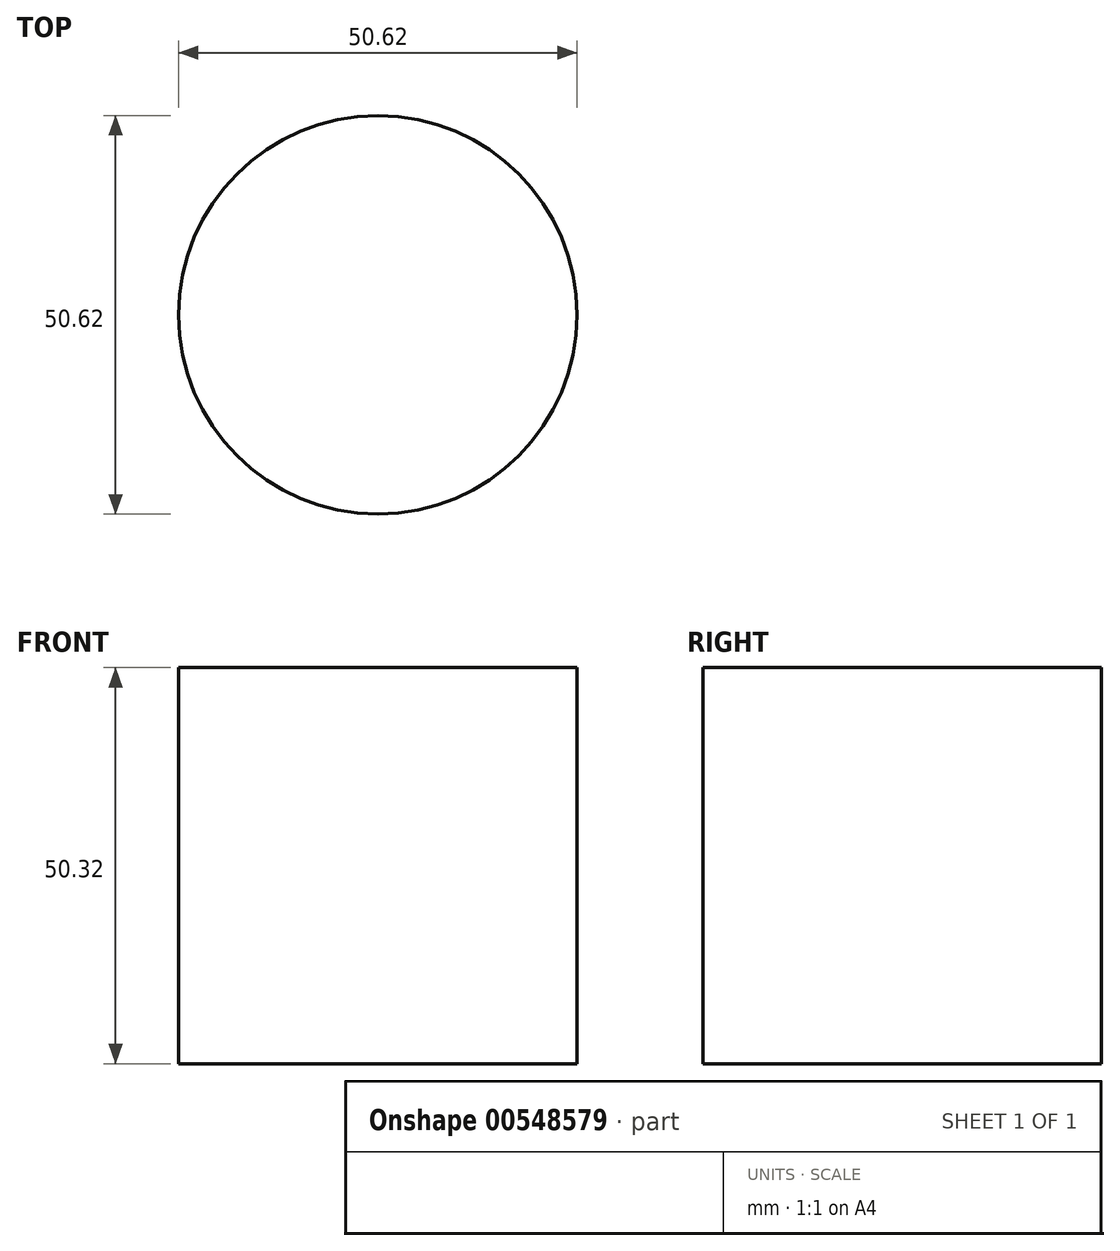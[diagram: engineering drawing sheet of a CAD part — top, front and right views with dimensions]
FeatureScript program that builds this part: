
annotation { "Feature Type Name" : "Feature", "Feature Type Description" : "" }
export const myFeature = defineFeature(function(context is Context, id is Id, definition is map)
    precondition{}
    {
        {
            var Q0;
            Q0=qCreatedBy(makeId("Front.planeOp"),FACE);
            var sketch = newSketch(context, id + "F0", { "sketchPlane" : qUnion([Q0])});
            skLineSegment(sketch, "E0.bottom", {"start": v(0, 25.16) * mm, "end": v(25.31, 25.16) * mm});
            skLineSegment(sketch, "E0.top", {"start": v(0, -25.16) * mm, "end": v(25.31, -25.16) * mm});
            skLineSegment(sketch, "E0.left", {"start": v(0, 25.16) * mm, "end": v(0, -25.16) * mm});
            skLineSegment(sketch, "E0.right", {"start": v(25.31, 25.16) * mm, "end": v(25.31, -25.16) * mm});
            skLineSegment(sketch, "E1", {"start": v(0, 42.63) * mm, "end": v(0, -40.86) * mm, "construction": true});
            skSolve(sketch);
        }
        {
            var Q0;
            Q0 = qSketchRegion(id + "F0", true);
            var Q1;
            Q1=sQuery(id+"F0.wireOp",EDGE,"E1");
            revolve(context, id + "F1", {"entities" : qUnion([Q0]), "axis" : qUnion([Q1]), "revolveType" : RevolveType.FULL});
        }
    });
